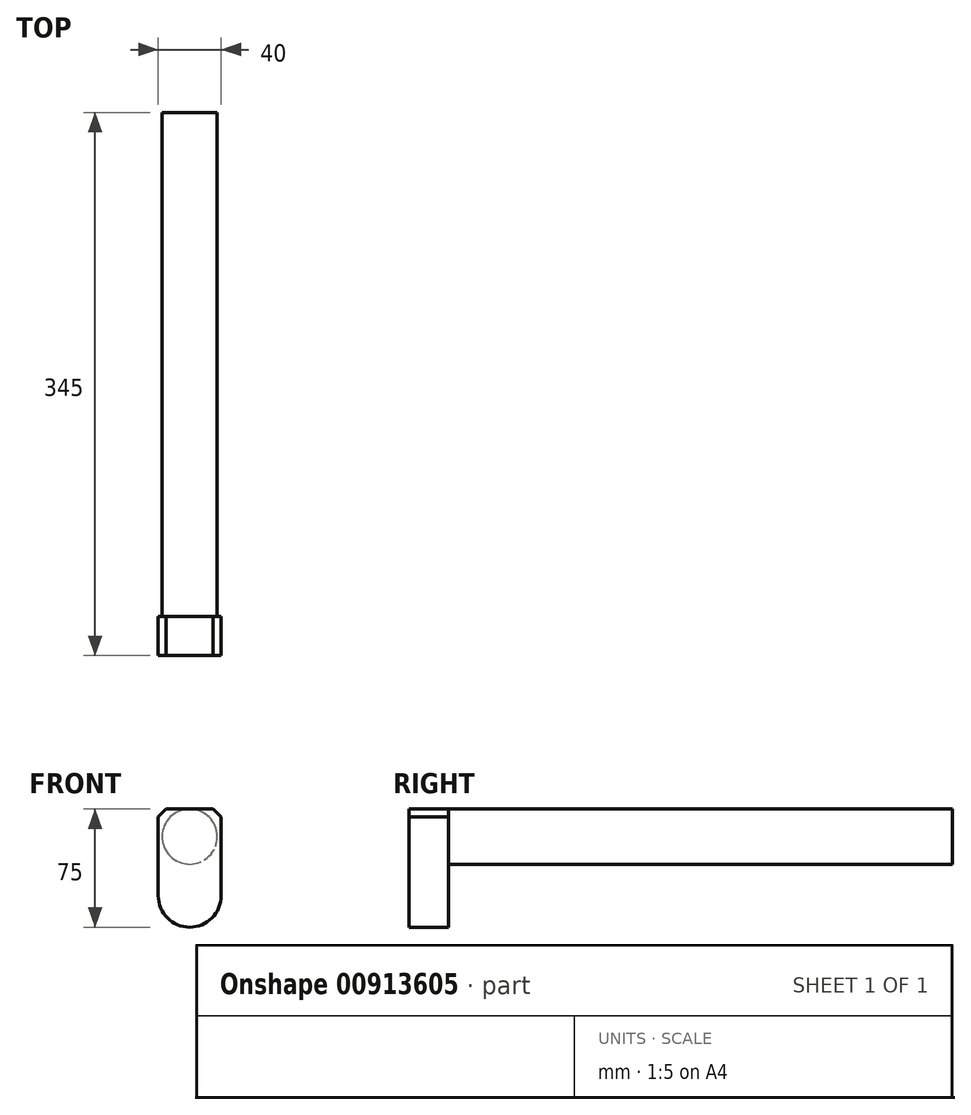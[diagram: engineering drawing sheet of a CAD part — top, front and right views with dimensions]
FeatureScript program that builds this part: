
annotation { "Feature Type Name" : "Feature", "Feature Type Description" : "" }
export const myFeature = defineFeature(function(context is Context, id is Id, definition is map)
    precondition{}
    {
        {
            var Q0;
            Q0=qCreatedBy(makeId("Front.planeOp"),FACE);
            var sketch = newSketch(context, id + "F0", { "sketchPlane" : qUnion([Q0])});
            skLineSegment(sketch, "E0.bottom", {"start": v(-20, 55) * mm, "end": v(20, 55) * mm});
            skLineSegment(sketch, "E0.top", {"start": v(-20, -20) * mm, "end": v(20, -20) * mm});
            skLineSegment(sketch, "E0.left", {"start": v(-20, 55) * mm, "end": v(-20, -20) * mm});
            skLineSegment(sketch, "E0.right", {"start": v(20, 55) * mm, "end": v(20, -20) * mm});
            skCircle(sketch, "E1", {"center": v(0, -20) * mm, "radius": 20 * mm, "construction": true});
            skLineSegment(sketch, "E2", {"start": v(0, -20) * mm, "end": v(0, 0) * mm});
            skCircle(sketch, "E3", {"center": v(0, 0) * mm, "radius": 20 * mm});
            skSolve(sketch);
        }
        {
            var Q0;
            {var subQ0=sQuery(id+"F0.wireOp",EDGE,"E0.bottom");Q0=makeQuery(id+"F0.imprint","IMPRINT",FACE,{"disambiguationData":[TD([[makeQuery(id+"F0.imprint","IMPRINT",EDGE,{"derivedFrom":subQ0}),-1.0]])]});}
            var Q1;
            {var subQ0=sQuery(id+"F0.wireOp",EDGE,"E3");var subQ1=makeQuery(id+"F0.imprint","INTERSECT",VERTEX,{"derivedFrom":[sQuery(id+"F0.wireOp",EDGE,"E0.left"),subQ0]});Q1=makeQuery(id+"F0.imprint","IMPRINT",FACE,{"disambiguationData":[TD([[makeQuery(id+"F0.imprint","IMPRINT",EDGE,{"disambiguationData":[TD([[subQ1,1.0]])],"derivedFrom":subQ0}),1.0]])]});}
            extrude(context, id + "F1", {"entities" : qUnion([Q0, Q1]), "depth" : 25 * mm});
        }
        {
            var Q0;
            {var subQ0=sQuery(id+"F0.wireOp",EDGE,"E0.bottom");Q0=makeQuery(id+"F0.imprint","IMPRINT",FACE,{"disambiguationData":[TD([[makeQuery(id+"F0.imprint","IMPRINT",EDGE,{"derivedFrom":subQ0}),-1.0]])]});}
            var sketch = newSketch(context, id + "F2", { "sketchPlane" : qUnion([Q0])});
            skCircle(sketch, "E4", {"center": v(0, 37.5) * mm, "radius": 17.5 * mm});
            skLineSegment(sketch, "E5", {"start": v(0, -20.52) * mm, "end": v(0, 37.5) * mm, "construction": true});
            skSolve(sketch);
        }
        {
            var Q0;
            Q0=qSketchRegion(id+"F2",true);
            extrude(context, id + "F3", {"entities" : qUnion([Q0]), "operationType" : NewBodyOperationType.ADD, "oppositeDirection" : true, "depth" : 320 * mm});
        }
        {
            var Q0;
            Q0=makeQuery(id+"F1.opExtrude","SWEPT_EDGE",EDGE,{"disambiguationData":[OSD([sQuery(id+"F0.wireOp",EDGE,"E0.bottom"),sQuery(id+"F0.wireOp",EDGE,"E0.right")])]});
            var Q1;
            Q1=makeQuery(id+"F1.opExtrude","SWEPT_EDGE",EDGE,{"disambiguationData":[OSD([sQuery(id+"F0.wireOp",EDGE,"E0.bottom"),sQuery(id+"F0.wireOp",EDGE,"E0.left")])]});
            chamfer(context, id + "F4", {"entities" : qUnion([Q0, Q1]), "width" : 5 * mm, "tangentPropagation" : true});
        }
    });
